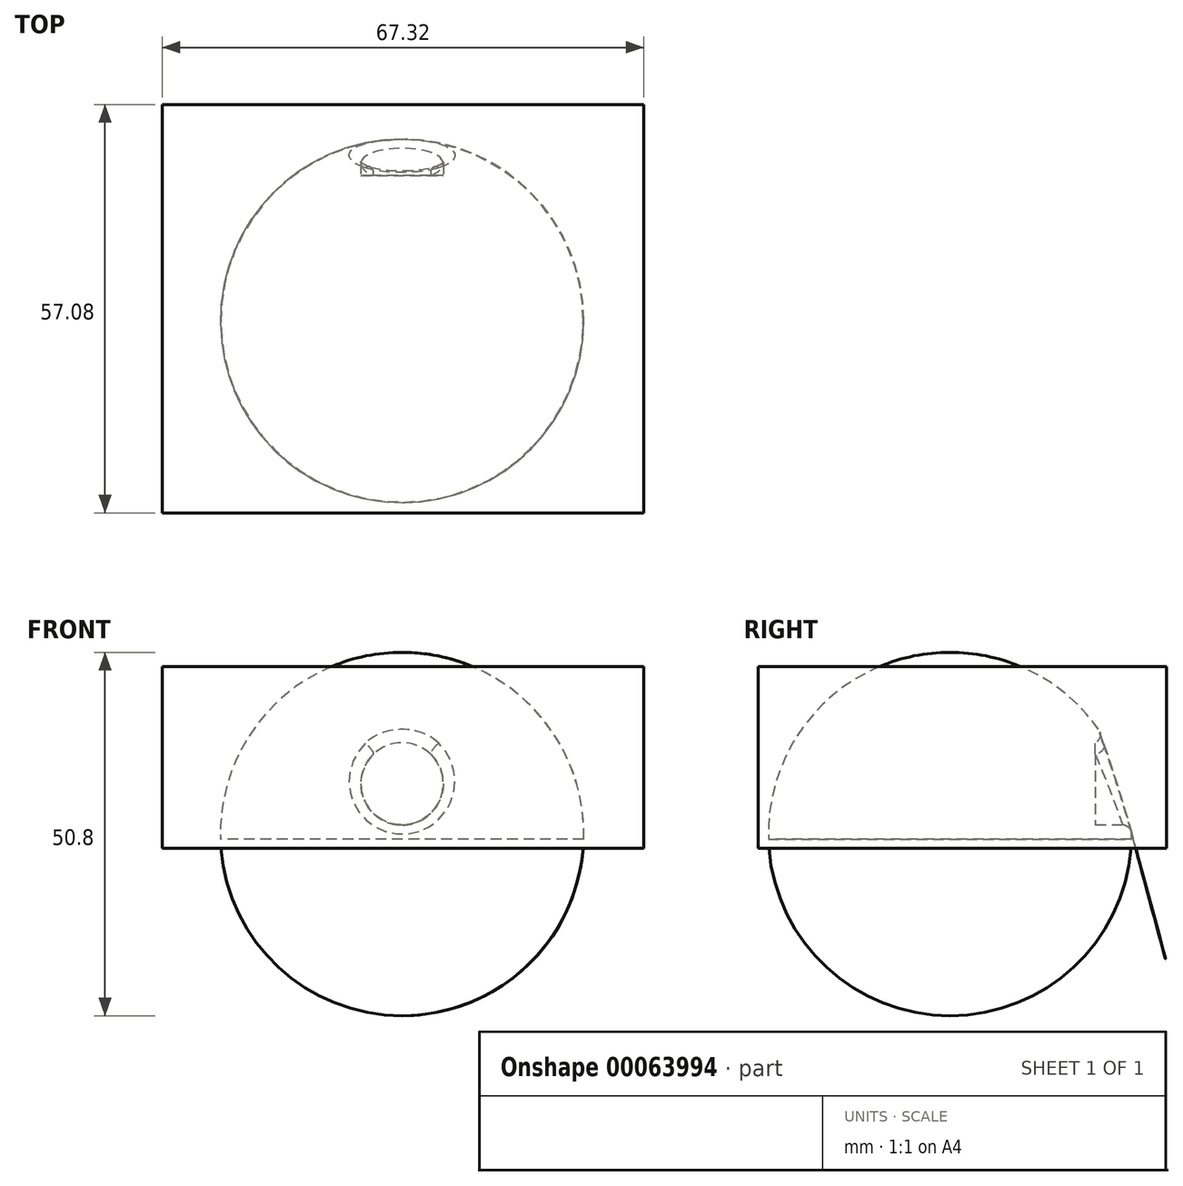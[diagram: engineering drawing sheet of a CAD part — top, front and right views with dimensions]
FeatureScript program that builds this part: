
annotation { "Feature Type Name" : "Feature", "Feature Type Description" : "" }
export const myFeature = defineFeature(function(context is Context, id is Id, definition is map)
    precondition{}
    {
        {
            var Q0;
            Q0=qCreatedBy(makeId("Top.planeOp"),FACE);
            var sketch = newSketch(context, id + "F0", { "sketchPlane" : qUnion([Q0])});
            skCircle(sketch, "E0", {"center": v(0, 0) * mm, "radius": 25.4 * mm});
            skSolve(sketch);
        }
        {
            var Q0;
            Q0=makeQuery(id+"F0.imprint","IMPRINT",FACE,{"disambiguationData":[TD([[makeQuery(id+"F0.imprint","IMPRINT",EDGE,{"derivedFrom":sQuery(id+"F0.wireOp",EDGE,"E0")}),1.0]])]});
            extrude(context, id + "F1", {"entities" : qUnion([Q0]), "depth" : 50.8 * mm});
        }
        {
            var Q0;
            Q0=makeQuery(id+"F1.opExtrude","CAP_EDGE",EDGE,{"disambiguationData":[OSD([sQuery(id+"F0.wireOp",EDGE,"E0")])],"isStart":false});
            fillet(context, id + "F2", {"entities" : qUnion([Q0]), "radius" : 25.4 * mm, "tangentPropagation" : true, "allowEdgeOverflow" : false});
        }
        {
            var Q0;
            Q0=makeQuery(id+"F1.opExtrude","CAP_EDGE",EDGE,{"disambiguationData":[OSD([sQuery(id+"F0.wireOp",EDGE,"E0")])],"isStart":true});
            fillet(context, id + "F3", {"entities" : qUnion([Q0]), "radius" : 25.4 * mm, "tangentPropagation" : true, "allowEdgeOverflow" : false});
        }
        {
            var Q0;
            Q0=qCreatedBy(makeId("Front.planeOp"),FACE);
            var sketch = newSketch(context, id + "F4", { "sketchPlane" : qUnion([Q0])});
            skCircle(sketch, "E1", {"center": v(0, 32.41) * mm, "radius": 5.76 * mm});
            skSolve(sketch);
        }
        {
            var Q0;
            Q0 = qSketchRegion(id + "F4", true);
            extrude(context, id + "F5", {"entities" : qUnion([Q0]), "operationType" : NewBodyOperationType.REMOVE, "oppositeDirection" : true, "depth" : 25.4 * mm});
        }
        {
            var Q0;
            Q0=qCreatedBy(makeId("Front.planeOp"),FACE);
            var sketch = newSketch(context, id + "F6", { "sketchPlane" : qUnion([Q0])});
            skCircle(sketch, "E2", {"center": v(0, 32.44) * mm, "radius": 5.8 * mm});
            skSolve(sketch);
        }
        {
            var Q0;
            Q0 = qSketchRegion(id + "F6", true);
            extrude(context, id + "F7", {"entities" : qUnion([Q0]), "operationType" : NewBodyOperationType.ADD, "oppositeDirection" : true, "depth" : 20.32 * mm});
        }
        {
            var Q0;
            Q0=makeQuery(id+"F5.boolean.opBoolean","INTERSECT",EDGE,{"derivedFrom":[makeQuery(id+"F2.opFillet","BLEND_FACE",FACE,{"disambiguationData":[OSD([sQuery(id+"F0.wireOp",EDGE,"E0")])]}),makeQuery(id+"F5.opExtrude","SWEPT_FACE",FACE,{"disambiguationData":[OSD([sQuery(id+"F4.wireOp",EDGE,"E1")])]})]});
            fillet(context, id + "F8", {"entities" : qUnion([Q0]), "radius" : 1.27 * mm, "tangentPropagation" : true, "allowEdgeOverflow" : false});
        }
        {
            var Q0;
            Q0=qCreatedBy(makeId("Right.planeOp"),FACE);
            var sketch = newSketch(context, id + "F9", { "sketchPlane" : qUnion([Q0])});
            skLineSegment(sketch, "E3", {"start": v(0, 0) * mm, "end": v(0, 55.5) * mm});
            skSolve(sketch);
        }
        {
            var Q0;
            Q0=qCreatedBy(makeId("Front.planeOp"),FACE);
            var sketch = newSketch(context, id + "F10", { "sketchPlane" : qUnion([Q0])});
            skLineSegment(sketch, "E4.bottom", {"start": v(0, 23.42) * mm, "end": v(33.62, 23.42) * mm});
            skLineSegment(sketch, "E4.top", {"start": v(0, 24.7) * mm, "end": v(33.62, 24.7) * mm});
            skLineSegment(sketch, "E4.left", {"start": v(0, 23.42) * mm, "end": v(0, 24.7) * mm});
            skLineSegment(sketch, "E4.right", {"start": v(33.62, 23.42) * mm, "end": v(33.62, 24.7) * mm});
            skSolve(sketch);
        }
        {
            var Q0;
            Q0 = qSketchRegion(id + "F10", true);
            var Q1;
            Q1=sQuery(id+"F9.wireOp",EDGE,"E3");
            revolve(context, id + "F11", {"operationType" : NewBodyOperationType.REMOVE, "entities" : qUnion([Q0]), "axis" : qUnion([Q1]), "revolveType" : RevolveType.FULL, "oppositeDirection" : true});
        }
        {
            var Q0;
            Q0=makeQuery(id+"F11.boolean.opBoolean","COPY",FACE,{"derivedFrom":makeQuery(id+"F11.opRevolve","SWEPT_FACE",FACE,{"disambiguationData":[OSD([sQuery(id+"F10.wireOp",EDGE,"E4.bottom")])]})});
            var sketch = newSketch(context, id + "F12", { "sketchPlane" : qUnion([Q0])});
            skLineSegment(sketch, "E5.bottom", {"start": v(-33.54, -26.83) * mm, "end": v(33.78, -26.83) * mm});
            skLineSegment(sketch, "E5.top", {"start": v(-33.54, 30.25) * mm, "end": v(33.78, 30.25) * mm});
            skLineSegment(sketch, "E5.left", {"start": v(-33.54, -26.83) * mm, "end": v(-33.54, 30.25) * mm});
            skLineSegment(sketch, "E5.right", {"start": v(33.78, -26.83) * mm, "end": v(33.78, 30.25) * mm});
            skSolve(sketch);
        }
        {
            var Q0;
            Q0 = qSketchRegion(id + "F12", true);
            extrude(context, id + "F13", {"entities" : qUnion([Q0]), "depth" : 25.4 * mm});
        }
    });
